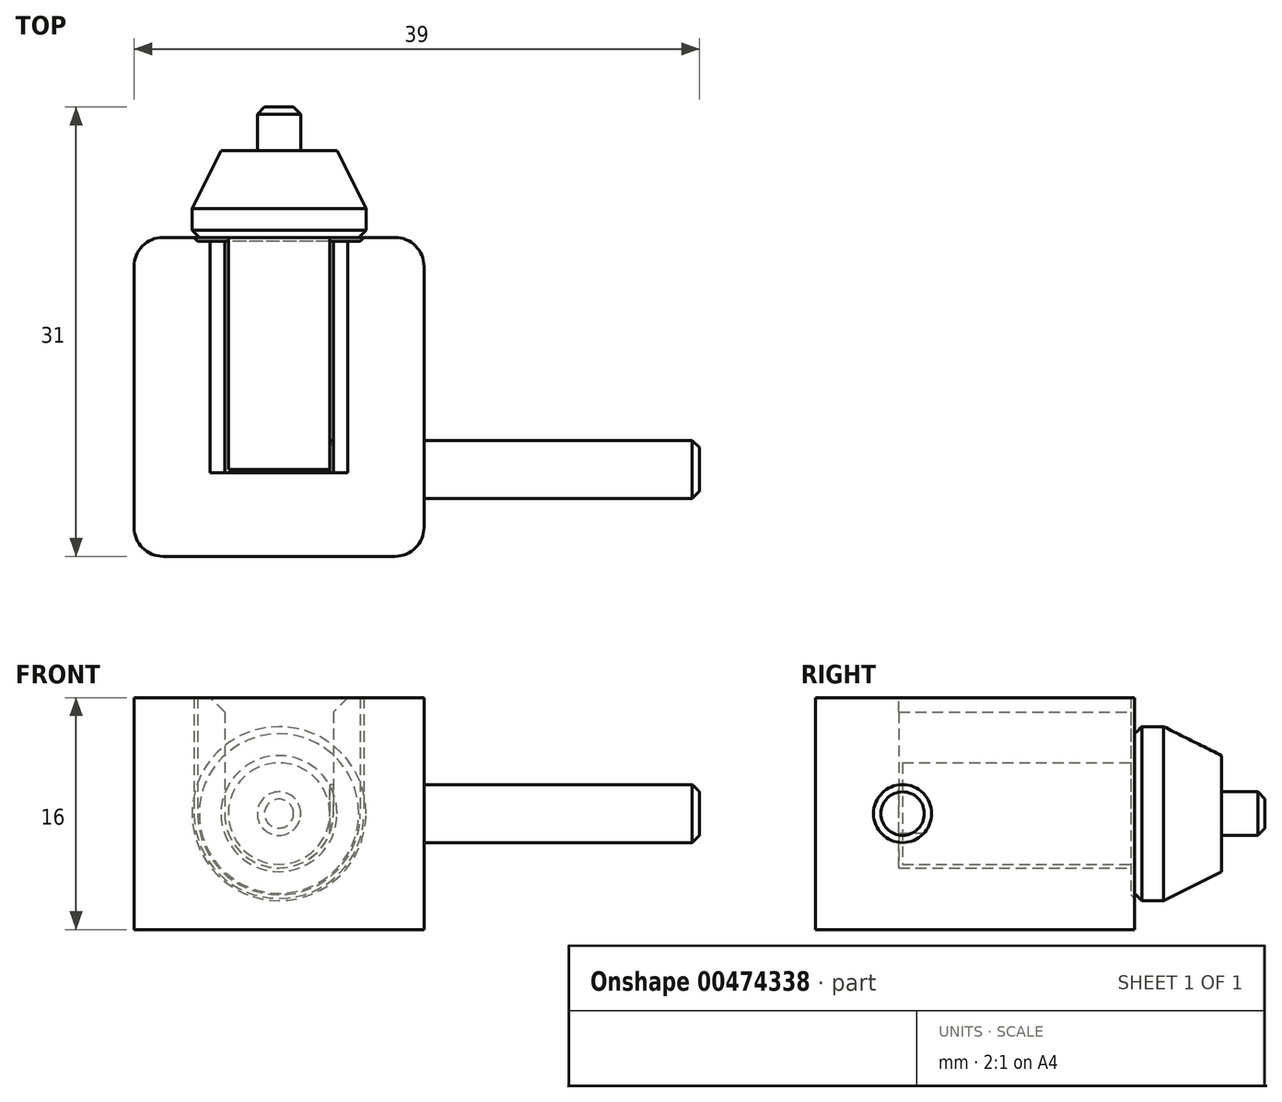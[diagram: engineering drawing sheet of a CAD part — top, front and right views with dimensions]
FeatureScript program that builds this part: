
annotation { "Feature Type Name" : "Feature", "Feature Type Description" : "" }
export const myFeature = defineFeature(function(context is Context, id is Id, definition is map)
    precondition{}
    {
        {
            var Q0;
            Q0=qCreatedBy(makeId("Top.planeOp"),FACE);
            var sketch = newSketch(context, id + "F0", { "sketchPlane" : qUnion([Q0])});
            skLineSegment(sketch, "E0", {"start": v(0, 0) * mm, "end": v(3.5, 0) * mm});
            skLineSegment(sketch, "E1", {"start": v(3.5, 0) * mm, "end": v(3.5, 22) * mm});
            skLineSegment(sketch, "E2", {"start": v(3.5, 22) * mm, "end": v(6, 22) * mm});
            skLineSegment(sketch, "E3", {"start": v(6, 22) * mm, "end": v(6, 24) * mm});
            skLineSegment(sketch, "E4", {"start": v(6, 24) * mm, "end": v(4, 28) * mm});
            skLineSegment(sketch, "E5", {"start": v(4, 28) * mm, "end": v(1.5, 28) * mm});
            skLineSegment(sketch, "E6", {"start": v(1.5, 28) * mm, "end": v(1.5, 31) * mm});
            skLineSegment(sketch, "E7", {"start": v(1.5, 31) * mm, "end": v(0, 31) * mm});
            skLineSegment(sketch, "E8", {"start": v(0, 31) * mm, "end": v(0, 0) * mm});
            skLineSegment(sketch, "E9.bottom", {"start": v(0, 6) * mm, "end": v(29, 6) * mm});
            skLineSegment(sketch, "E9.top", {"start": v(0, 4) * mm, "end": v(29, 4) * mm});
            skLineSegment(sketch, "E9.left", {"start": v(0, 6) * mm, "end": v(0, 4) * mm});
            skLineSegment(sketch, "E9.right", {"start": v(29, 6) * mm, "end": v(29, 4) * mm});
            skLineSegment(sketch, "E10.MirrorCS", {"start": v(0, 6) * mm, "end": v(-29, 6) * mm});
            skLineSegment(sketch, "E11.MirrorCS", {"start": v(0, 4) * mm, "end": v(-29, 4) * mm});
            skLineSegment(sketch, "E12.MirrorCS", {"start": v(-29, 6) * mm, "end": v(-29, 4) * mm});
            skSolve(sketch);
        }
        {
            var Q0;
            {var subQ0=sQuery(id+"F0.wireOp",EDGE,"E2");Q0=makeQuery(id+"F0.imprint","IMPRINT",FACE,{"disambiguationData":[TD([[makeQuery(id+"F0.imprint","IMPRINT",EDGE,{"derivedFrom":subQ0}),1.0]])]});}
            var Q1;
            {var subQ5=sQuery(id+"F0.wireOp",EDGE,"E9.left");Q1=makeQuery(id+"F0.imprint","IMPRINT",FACE,{"disambiguationData":[TD([[makeQuery(id+"F0.imprint","IMPRINT",EDGE,{"derivedFrom":subQ5}),1.0]])]});}
            var Q2;
            {var subQ0=sQuery(id+"F0.wireOp",EDGE,"E0");Q2=makeQuery(id+"F0.imprint","IMPRINT",FACE,{"disambiguationData":[TD([[makeQuery(id+"F0.imprint","IMPRINT",EDGE,{"derivedFrom":subQ0}),1.0]])]});}
            var Q3;
            Q3=sQuery(id+"F0.wireOp",EDGE,"E8");
            revolve(context, id + "F1", {"entities" : qUnion([Q0, Q1, Q2]), "axis" : qUnion([Q3]), "revolveType" : RevolveType.FULL});
        }
        {
            var Q0;
            {var subQ5=sQuery(id+"F0.wireOp",EDGE,"E9.right");Q0=makeQuery(id+"F0.imprint","IMPRINT",FACE,{"disambiguationData":[TD([[makeQuery(id+"F0.imprint","IMPRINT",EDGE,{"derivedFrom":subQ5}),-1.0]])]});}
            var Q1;
            {var subQ5=sQuery(id+"F0.wireOp",EDGE,"E9.left");Q1=makeQuery(id+"F0.imprint","IMPRINT",FACE,{"disambiguationData":[TD([[makeQuery(id+"F0.imprint","IMPRINT",EDGE,{"derivedFrom":subQ5}),1.0]])]});}
            var Q2;
            Q2=makeQuery(id+"F0.imprint","IMPRINT",FACE,{"disambiguationData":[TD([[makeQuery(id+"F0.imprint","IMPRINT",EDGE,{"derivedFrom":sQuery(id+"F0.wireOp",EDGE,"E9.left")}),-1.0]])]});
            var Q3;
            Q3=sQuery(id+"F0.wireOp",EDGE,"E9.bottom");
            revolve(context, id + "F2", {"operationType" : NewBodyOperationType.ADD, "entities" : qUnion([Q0, Q1, Q2]), "axis" : qUnion([Q3]), "revolveType" : RevolveType.FULL});
        }
        {
            var Q0;
            Q0=makeQuery(id+"F2.opRevolve","SWEPT_EDGE",EDGE,{"disambiguationData":[OSD([sQuery(id+"F0.wireOp",EDGE,"E11.MirrorCS"),sQuery(id+"F0.wireOp",EDGE,"E12.MirrorCS")])]});
            var Q1;
            Q1=makeQuery(id+"F2.opRevolve","SWEPT_EDGE",EDGE,{"disambiguationData":[OSD([sQuery(id+"F0.wireOp",EDGE,"E9.top"),sQuery(id+"F0.wireOp",EDGE,"E9.right")])]});
            var Q2;
            Q2=makeQuery(id+"F1.opRevolve","SWEPT_EDGE",EDGE,{"disambiguationData":[OSD([sQuery(id+"F0.wireOp",EDGE,"E2"),sQuery(id+"F0.wireOp",EDGE,"E3")])]});
            var Q3;
            Q3=makeQuery(id+"F1.opRevolve","SWEPT_EDGE",EDGE,{"disambiguationData":[OSD([sQuery(id+"F0.wireOp",EDGE,"E6"),sQuery(id+"F0.wireOp",EDGE,"E7")])]});
            var Q4;
            Q4=makeQuery(id+"F1.opRevolve","SWEPT_EDGE",EDGE,{"disambiguationData":[OSD([sQuery(id+"F0.wireOp",EDGE,"E0"),sQuery(id+"F0.wireOp",EDGE,"E1")])]});
            chamfer(context, id + "F3", {"entities" : qUnion([Q0, Q1, Q2, Q3, Q4]), "width" : 0.5 * mm, "tangentPropagation" : true});
        }
        {
            var Q0;
            Q0=qCreatedBy(makeId("Top.planeOp"),FACE);
            var sketch = newSketch(context, id + "F4", { "sketchPlane" : qUnion([Q0])});
            skPoint(sketch, "E13.0", {"position": v(6, 22) * mm});
            skLineSegment(sketch, "E14.bottom", {"start": v(0, 0) * mm, "end": v(8, 0) * mm});
            skLineSegment(sketch, "E14.top", {"start": v(0, 22) * mm, "end": v(8, 22) * mm});
            skLineSegment(sketch, "E14.left", {"start": v(0, 0) * mm, "end": v(0, 22) * mm});
            skLineSegment(sketch, "E14.right", {"start": v(10, 2) * mm, "end": v(10, 20) * mm});
            skPoint(sketch, "E15.visualSharp", {"position": v(10, 22) * mm});
            skArc(sketch, "E15.filletArc", {"start": v(10, 20) * mm, "mid": v(9.41, 21.41) * mm, "end": v(8, 22) * mm});
            skPoint(sketch, "E16.visualSharp", {"position": v(10, 0) * mm});
            skArc(sketch, "E16.filletArc", {"start": v(8, 0) * mm, "mid": v(9.41, 0.59) * mm, "end": v(10, 2) * mm});
            skLineSegment(sketch, "E17.MirrorCS", {"start": v(0, 22) * mm, "end": v(-8, 22) * mm});
            skArc(sketch, "E18.MirrorCS", {"start": v(-10, 20) * mm, "mid": v(-9.41, 21.41) * mm, "end": v(-8, 22) * mm});
            skLineSegment(sketch, "E19.MirrorCS", {"start": v(-10, 2) * mm, "end": v(-10, 20) * mm});
            skArc(sketch, "E20.MirrorCS", {"start": v(-8, 0) * mm, "mid": v(-9.41, 0.59) * mm, "end": v(-10, 2) * mm});
            skLineSegment(sketch, "E21.MirrorCS", {"start": v(0, 0) * mm, "end": v(-8, 0) * mm});
            skSolve(sketch);
        }
        {
            var Q0;
            Q0=makeQuery(id+"F4.imprint","IMPRINT",FACE,{"disambiguationData":[TD([[makeQuery(id+"F4.imprint","IMPRINT",EDGE,{"derivedFrom":sQuery(id+"F4.wireOp",EDGE,"E14.left")}),1.0]])]});
            var Q1;
            Q1=makeQuery(id+"F4.imprint","IMPRINT",FACE,{"disambiguationData":[TD([[makeQuery(id+"F4.imprint","IMPRINT",EDGE,{"derivedFrom":sQuery(id+"F4.wireOp",EDGE,"E14.bottom")}),1.0]])]});
            extrude(context, id + "F5", {"entities" : qUnion([Q0, Q1]), "oppositeDirection" : true, "depth" : 8 * mm});
        }
        {
            var Q0;
            Q0=makeQuery(id+"F1.opRevolve","SWEPT_BODY",BODY,{"disambiguationData":[OSD([sQuery(id+"F0.wireOp",EDGE,"E0"),sQuery(id+"F0.wireOp",EDGE,"E1"),sQuery(id+"F0.wireOp",EDGE,"E2"),sQuery(id+"F0.wireOp",EDGE,"E3"),sQuery(id+"F0.wireOp",EDGE,"E4"),sQuery(id+"F0.wireOp",EDGE,"E5"),sQuery(id+"F0.wireOp",EDGE,"E6"),sQuery(id+"F0.wireOp",EDGE,"E7"),sQuery(id+"F0.wireOp",EDGE,"E8"),sQuery(id+"F0.wireOp",EDGE,"E9.left")])]});
            var Q1;
            Q1=makeQuery(id+"F5.opExtrude","SWEPT_BODY",BODY,{"disambiguationData":[OSD([sQuery(id+"F4.wireOp",EDGE,"E14.bottom"),sQuery(id+"F4.wireOp",EDGE,"E14.top"),sQuery(id+"F4.wireOp",EDGE,"E14.right"),sQuery(id+"F4.wireOp",EDGE,"E15.filletArc"),sQuery(id+"F4.wireOp",EDGE,"E16.filletArc"),sQuery(id+"F4.wireOp",EDGE,"E17.MirrorCS"),sQuery(id+"F4.wireOp",EDGE,"E18.MirrorCS"),sQuery(id+"F4.wireOp",EDGE,"E19.MirrorCS"),sQuery(id+"F4.wireOp",EDGE,"E20.MirrorCS"),sQuery(id+"F4.wireOp",EDGE,"E21.MirrorCS")])]});
            booleanBodies(context, id + "F6", {"operationType" : BooleanOperationType.SUBTRACTION, "tools" : qUnion([Q0]), "targets" : qUnion([Q1]), "offset" : true, "offsetAll" : true, "offsetDistance" : 0.25 * mm, "keepTools" : true});
        }
        {
            var Q0;
            {var subQ0=sQuery(id+"F4.wireOp",EDGE,"E15.filletArc");var subQ3=sQuery(id+"F4.wireOp",EDGE,"E14.right");var subQ4=sQuery(id+"F4.wireOp",EDGE,"E17.MirrorCS");var subQ5=sQuery(id+"F4.wireOp",EDGE,"E14.top");Q0=makeQuery(id+"F6.tempBoolean.opBoolean","SPLIT",FACE,{"disambiguationData":[TD([makeQuery(id+"F5.opExtrude","SWEPT_FACE",FACE,{"disambiguationData":[OSD([subQ0])]})])],"derivedFrom":makeQuery(id+"F5.opExtrude","CAP_FACE",FACE,{"disambiguationData":[OSD([sQuery(id+"F4.wireOp",EDGE,"E14.bottom"),subQ5,subQ3,subQ0,sQuery(id+"F4.wireOp",EDGE,"E16.filletArc"),subQ4,sQuery(id+"F4.wireOp",EDGE,"E18.MirrorCS"),sQuery(id+"F4.wireOp",EDGE,"E19.MirrorCS"),sQuery(id+"F4.wireOp",EDGE,"E20.MirrorCS"),sQuery(id+"F4.wireOp",EDGE,"E21.MirrorCS")])],"isStart":true})});}
            var Q1;
            {var subQ1=sQuery(id+"F4.wireOp",EDGE,"E18.MirrorCS");var subQ3=sQuery(id+"F4.wireOp",EDGE,"E19.MirrorCS");var subQ4=sQuery(id+"F4.wireOp",EDGE,"E17.MirrorCS");var subQ5=sQuery(id+"F4.wireOp",EDGE,"E14.top");Q1=makeQuery(id+"F6.tempBoolean.opBoolean","SPLIT",FACE,{"disambiguationData":[TD([makeQuery(id+"F5.opExtrude","SWEPT_FACE",FACE,{"disambiguationData":[OSD([subQ1])]})])],"derivedFrom":makeQuery(id+"F5.opExtrude","CAP_FACE",FACE,{"disambiguationData":[OSD([sQuery(id+"F4.wireOp",EDGE,"E14.bottom"),subQ5,sQuery(id+"F4.wireOp",EDGE,"E14.right"),sQuery(id+"F4.wireOp",EDGE,"E15.filletArc"),sQuery(id+"F4.wireOp",EDGE,"E16.filletArc"),subQ4,subQ1,subQ3,sQuery(id+"F4.wireOp",EDGE,"E20.MirrorCS"),sQuery(id+"F4.wireOp",EDGE,"E21.MirrorCS")])],"isStart":true})});}
            var Q2;
            {var subQ0=sQuery(id+"F4.wireOp",EDGE,"E20.MirrorCS");var subQ3=sQuery(id+"F4.wireOp",EDGE,"E19.MirrorCS");var subQ4=sQuery(id+"F4.wireOp",EDGE,"E21.MirrorCS");var subQ5=sQuery(id+"F4.wireOp",EDGE,"E14.bottom");Q2=makeQuery(id+"F6.tempBoolean.opBoolean","SPLIT",FACE,{"disambiguationData":[TD([makeQuery(id+"F5.opExtrude","SWEPT_FACE",FACE,{"disambiguationData":[OSD([subQ0])]})])],"derivedFrom":makeQuery(id+"F5.opExtrude","CAP_FACE",FACE,{"disambiguationData":[OSD([subQ5,sQuery(id+"F4.wireOp",EDGE,"E14.top"),sQuery(id+"F4.wireOp",EDGE,"E14.right"),sQuery(id+"F4.wireOp",EDGE,"E15.filletArc"),sQuery(id+"F4.wireOp",EDGE,"E16.filletArc"),sQuery(id+"F4.wireOp",EDGE,"E17.MirrorCS"),sQuery(id+"F4.wireOp",EDGE,"E18.MirrorCS"),subQ3,subQ0,subQ4])],"isStart":true})});}
            var Q3;
            {var subQ1=sQuery(id+"F4.wireOp",EDGE,"E16.filletArc");var subQ2=sQuery(id+"F4.wireOp",EDGE,"E14.right");var subQ3=sQuery(id+"F4.wireOp",EDGE,"E21.MirrorCS");var subQ4=sQuery(id+"F4.wireOp",EDGE,"E14.bottom");Q3=makeQuery(id+"F6.tempBoolean.opBoolean","SPLIT",FACE,{"disambiguationData":[TD([makeQuery(id+"F5.opExtrude","SWEPT_FACE",FACE,{"disambiguationData":[OSD([subQ1])]})])],"derivedFrom":makeQuery(id+"F5.opExtrude","CAP_FACE",FACE,{"disambiguationData":[OSD([subQ4,sQuery(id+"F4.wireOp",EDGE,"E14.top"),subQ2,sQuery(id+"F4.wireOp",EDGE,"E15.filletArc"),subQ1,sQuery(id+"F4.wireOp",EDGE,"E17.MirrorCS"),sQuery(id+"F4.wireOp",EDGE,"E18.MirrorCS"),sQuery(id+"F4.wireOp",EDGE,"E19.MirrorCS"),sQuery(id+"F4.wireOp",EDGE,"E20.MirrorCS"),subQ3])],"isStart":true})});}
            extrude(context, id + "F7", {"entities" : qUnion([Q0, Q1, Q2, Q3]), "operationType" : NewBodyOperationType.ADD, "depth" : 8 * mm});
        }
        {
            var Q0;
            {var subQ0=sQuery(id+"F0.wireOp",EDGE,"E1");var subQ1=sQuery(id+"F4.wireOp",EDGE,"E21.MirrorCS");var subQ2=sQuery(id+"F4.wireOp",EDGE,"E20.MirrorCS");var subQ3=sQuery(id+"F4.wireOp",EDGE,"E19.MirrorCS");var subQ4=sQuery(id+"F4.wireOp",EDGE,"E18.MirrorCS");var subQ5=sQuery(id+"F4.wireOp",EDGE,"E17.MirrorCS");var subQ6=sQuery(id+"F4.wireOp",EDGE,"E16.filletArc");var subQ7=sQuery(id+"F4.wireOp",EDGE,"E15.filletArc");var subQ8=sQuery(id+"F4.wireOp",EDGE,"E14.right");var subQ9=sQuery(id+"F4.wireOp",EDGE,"E14.top");var subQ10=sQuery(id+"F4.wireOp",EDGE,"E14.bottom");Q0=makeQuery(id+"F7.opExtrude","CAP_EDGE",EDGE,{"disambiguationData":[OSD([subQ0,subQ10,subQ9,subQ8,subQ7,subQ6,subQ5,subQ4,subQ3,subQ2,subQ1]),TDD([makeQuery(id+"F6.tempBoolean.opBoolean","INTERSECT",EDGE,{"disambiguationData":[OD(2.0)],"derivedFrom":[makeQuery(id+"F5.opExtrude","CAP_FACE",FACE,{"disambiguationData":[OSD([subQ10,subQ9,subQ8,subQ7,subQ6,subQ5,subQ4,subQ3,subQ2,subQ1])],"isStart":true}),makeQuery(id+"F6.offsetTempBody.opPattern","COPY",FACE,{"derivedFrom":makeQuery(id+"F1.opRevolve","SWEPT_FACE",FACE,{"disambiguationData":[OSD([subQ0])]}),"instanceName":"1"})]})])],"isStart":false});}
            var Q1;
            {var subQ0=sQuery(id+"F0.wireOp",EDGE,"E1");var subQ1=sQuery(id+"F4.wireOp",EDGE,"E21.MirrorCS");var subQ2=sQuery(id+"F4.wireOp",EDGE,"E20.MirrorCS");var subQ3=sQuery(id+"F4.wireOp",EDGE,"E19.MirrorCS");var subQ4=sQuery(id+"F4.wireOp",EDGE,"E18.MirrorCS");var subQ5=sQuery(id+"F4.wireOp",EDGE,"E17.MirrorCS");var subQ6=sQuery(id+"F4.wireOp",EDGE,"E16.filletArc");var subQ7=sQuery(id+"F4.wireOp",EDGE,"E15.filletArc");var subQ8=sQuery(id+"F4.wireOp",EDGE,"E14.right");var subQ9=sQuery(id+"F4.wireOp",EDGE,"E14.top");var subQ10=sQuery(id+"F4.wireOp",EDGE,"E14.bottom");Q1=makeQuery(id+"F7.opExtrude","CAP_EDGE",EDGE,{"disambiguationData":[OSD([subQ0,subQ10,subQ9,subQ8,subQ7,subQ6,subQ5,subQ4,subQ3,subQ2,subQ1]),TDD([makeQuery(id+"F6.tempBoolean.opBoolean","INTERSECT",EDGE,{"disambiguationData":[OD(3.0)],"derivedFrom":[makeQuery(id+"F5.opExtrude","CAP_FACE",FACE,{"disambiguationData":[OSD([subQ10,subQ9,subQ8,subQ7,subQ6,subQ5,subQ4,subQ3,subQ2,subQ1])],"isStart":true}),makeQuery(id+"F6.offsetTempBody.opPattern","COPY",FACE,{"derivedFrom":makeQuery(id+"F1.opRevolve","SWEPT_FACE",FACE,{"disambiguationData":[OSD([subQ0])]}),"instanceName":"1"})]})])],"isStart":false});}
            var Q2;
            {var subQ0=sQuery(id+"F0.wireOp",EDGE,"E11.MirrorCS");var subQ1=sQuery(id+"F0.wireOp",EDGE,"E9.top");var subQ2=sQuery(id+"F4.wireOp",EDGE,"E21.MirrorCS");var subQ3=sQuery(id+"F4.wireOp",EDGE,"E20.MirrorCS");var subQ4=sQuery(id+"F4.wireOp",EDGE,"E19.MirrorCS");var subQ5=sQuery(id+"F4.wireOp",EDGE,"E18.MirrorCS");var subQ6=sQuery(id+"F4.wireOp",EDGE,"E17.MirrorCS");var subQ7=sQuery(id+"F4.wireOp",EDGE,"E16.filletArc");var subQ8=sQuery(id+"F4.wireOp",EDGE,"E15.filletArc");var subQ9=sQuery(id+"F4.wireOp",EDGE,"E14.right");var subQ10=sQuery(id+"F4.wireOp",EDGE,"E14.top");var subQ11=sQuery(id+"F4.wireOp",EDGE,"E14.bottom");Q2=makeQuery(id+"F7.opExtrude","CAP_EDGE",EDGE,{"disambiguationData":[OSD([subQ1,subQ0,subQ11,subQ10,subQ9,subQ8,subQ7,subQ6,subQ5,subQ4,subQ3,subQ2]),TDD([makeQuery(id+"F6.tempBoolean.opBoolean","INTERSECT",EDGE,{"disambiguationData":[OD(1.0)],"derivedFrom":[makeQuery(id+"F5.opExtrude","CAP_FACE",FACE,{"disambiguationData":[OSD([subQ11,subQ10,subQ9,subQ8,subQ7,subQ6,subQ5,subQ4,subQ3,subQ2])],"isStart":true}),makeQuery(id+"F6.offsetTempBody.opPattern","COPY",FACE,{"derivedFrom":makeQuery(id+"F2.boolean.opBoolean","SPLIT",FACE,{"disambiguationData":[TD([makeQuery(id+"F2.opRevolve","SWEPT_FACE",FACE,{"disambiguationData":[OSD([sQuery(id+"F0.wireOp",EDGE,"E12.MirrorCS")])]})])],"derivedFrom":makeQuery(id+"F2.opRevolve","SWEPT_FACE",FACE,{"disambiguationData":[OSD([subQ1,subQ0])]})}),"instanceName":"1"})]})])],"isStart":false});}
            var Q3;
            {var subQ0=sQuery(id+"F0.wireOp",EDGE,"E11.MirrorCS");var subQ1=sQuery(id+"F0.wireOp",EDGE,"E9.top");var subQ2=sQuery(id+"F4.wireOp",EDGE,"E21.MirrorCS");var subQ3=sQuery(id+"F4.wireOp",EDGE,"E20.MirrorCS");var subQ4=sQuery(id+"F4.wireOp",EDGE,"E19.MirrorCS");var subQ5=sQuery(id+"F4.wireOp",EDGE,"E18.MirrorCS");var subQ6=sQuery(id+"F4.wireOp",EDGE,"E17.MirrorCS");var subQ7=sQuery(id+"F4.wireOp",EDGE,"E16.filletArc");var subQ8=sQuery(id+"F4.wireOp",EDGE,"E15.filletArc");var subQ9=sQuery(id+"F4.wireOp",EDGE,"E14.right");var subQ10=sQuery(id+"F4.wireOp",EDGE,"E14.top");var subQ11=sQuery(id+"F4.wireOp",EDGE,"E14.bottom");Q3=makeQuery(id+"F7.opExtrude","CAP_EDGE",EDGE,{"disambiguationData":[OSD([subQ1,subQ0,subQ11,subQ10,subQ9,subQ8,subQ7,subQ6,subQ5,subQ4,subQ3,subQ2]),TDD([makeQuery(id+"F6.tempBoolean.opBoolean","INTERSECT",EDGE,{"disambiguationData":[OD(1.0)],"derivedFrom":[makeQuery(id+"F5.opExtrude","CAP_FACE",FACE,{"disambiguationData":[OSD([subQ11,subQ10,subQ9,subQ8,subQ7,subQ6,subQ5,subQ4,subQ3,subQ2])],"isStart":true}),makeQuery(id+"F6.offsetTempBody.opPattern","COPY",FACE,{"derivedFrom":makeQuery(id+"F2.boolean.opBoolean","SPLIT",FACE,{"disambiguationData":[TD([makeQuery(id+"F2.opRevolve","SWEPT_FACE",FACE,{"disambiguationData":[OSD([sQuery(id+"F0.wireOp",EDGE,"E9.right")])]})])],"derivedFrom":makeQuery(id+"F2.opRevolve","SWEPT_FACE",FACE,{"disambiguationData":[OSD([subQ1,subQ0])]})}),"instanceName":"1"})]})])],"isStart":false});}
            chamfer(context, id + "F8", {"entities" : qUnion([Q0, Q1, Q2, Q3]), "width" : 1 * mm, "tangentPropagation" : true});
        }
    });
